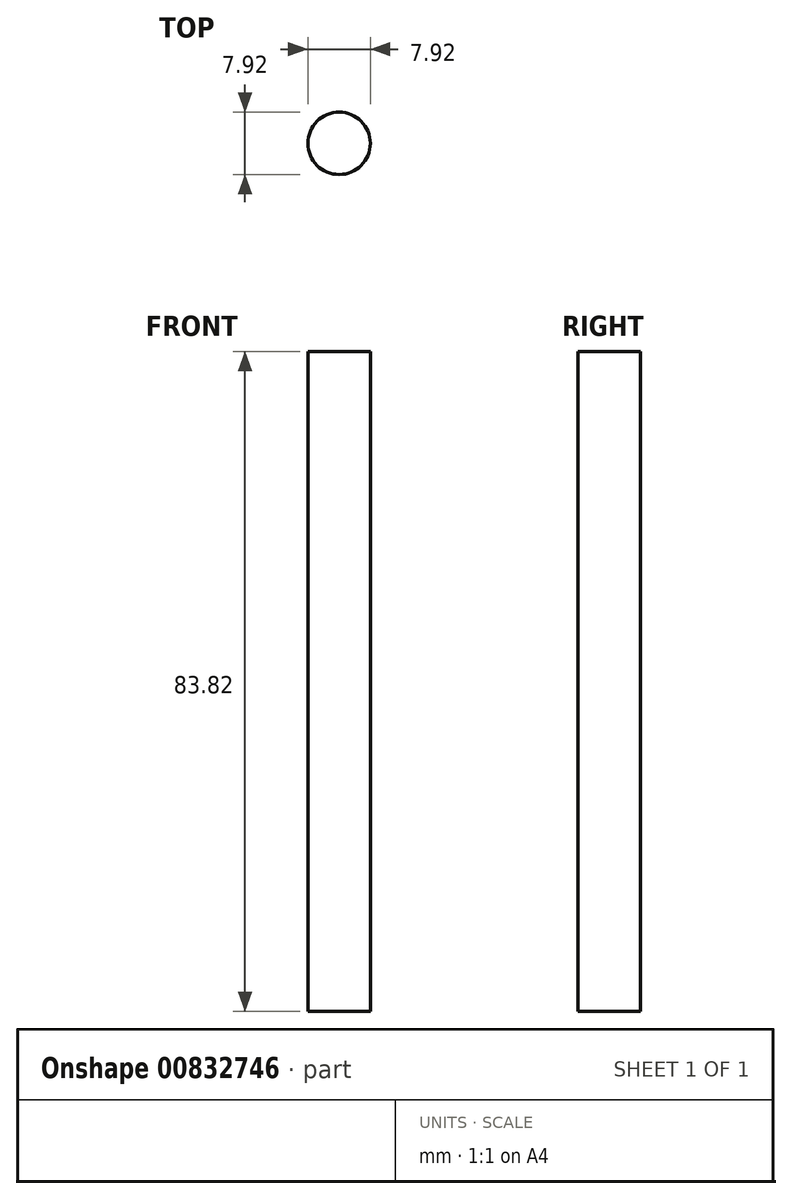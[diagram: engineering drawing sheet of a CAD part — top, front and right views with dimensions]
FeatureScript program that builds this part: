
annotation { "Feature Type Name" : "Feature", "Feature Type Description" : "" }
export const myFeature = defineFeature(function(context is Context, id is Id, definition is map)
    precondition{}
    {
        {
            var Q0;
            Q0=qCreatedBy(makeId("Top.planeOp"),FACE);
            var sketch = newSketch(context, id + "F0", { "sketchPlane" : qUnion([Q0])});
            skCircle(sketch, "E0", {"center": v(0, 0) * mm, "radius": 3.96 * mm});
            skSolve(sketch);
        }
        {
            var Q0;
            Q0 = qSketchRegion(id + "F0", true);
            extrude(context, id + "F1", {"entities" : qUnion([Q0]), "depth" : 83.82 * mm, "offsetDistance" : 25.4 * mm, "symmetric" : true});
        }
    });
